# Revit family: Varmax Twin 780
name_source: partatom
category: Mechanical Equipment
revit_build: Autodesk Revit 2014 (Build: 20130308_1515(x64)
units: mm (PartAtom-declared; Revit-internal decimal feet)

## types (1)
- Varmax Twin 780 - Caldera de pie de condensación a gas 830 kW y 6 bar (2/3 tomas)
    Altura = 2023 mm  [stored 6.63714 ft]
    Ancho = 2259 mm
    Ancho total = 2749 mm  [stored 9.01903 ft]
    Assembly Code = D3020100
    Configuración = 2 y 3 tomas
    Consumo eléctrico máximo = 960 W
    Description = Unidad térmica de condensación para gas natural Ygnis modelo Varmax 780,  potencia útil (50/30 ºC) de 830 kW. Fabricada en acero inoxidable de alta calidad AISI 316 L. Quemador modulante desde el 10% de la potencia. Rendimiento hasta el 108 ,9%. Clase 5 de NOx. Dimensiones (Altura x Ancho x Largo): 2023 x 2259 x 2114 mm. Peso en vacío: 1240 kg. Presión máxima de servicio: 6 bar. Configuración a 2 y 3 tomas.
    Diametro = 300 mm  [stored 0.984252 ft]
    Dist. = 450 mm
    Empresa creadora del BIM = ACAE
    Manufacturer = Atlantic
    Model = Varmax Twin 780
    Mínimo = 45 mm
    Peso en vacío = 1240 kg
    Potencia útil (50/30 ºC) = 830 kW
    Potencia útil a 80/60 ºC = 762 kW
    Presión máxima de servicio = 6 bar
    Profundidad = 2114 mm  [stored 6.9357 ft]
    Rendimiento mínimo al 100% de = 97,8%
    Rendimiento mínimo al 30% de carga = 108,9%
    Tipo de combustible = Gas natural (G20)
    URL = http://www.ygnis.es
    Volumen de agua = 574 L

note: [stored X ft] marks values corroborated as IEEE doubles in the binary element streams (Revit-internal decimal feet)

## geometry (parser evidence)
native form markers: Sweep x2
no freeform markers — native parametric forms only
